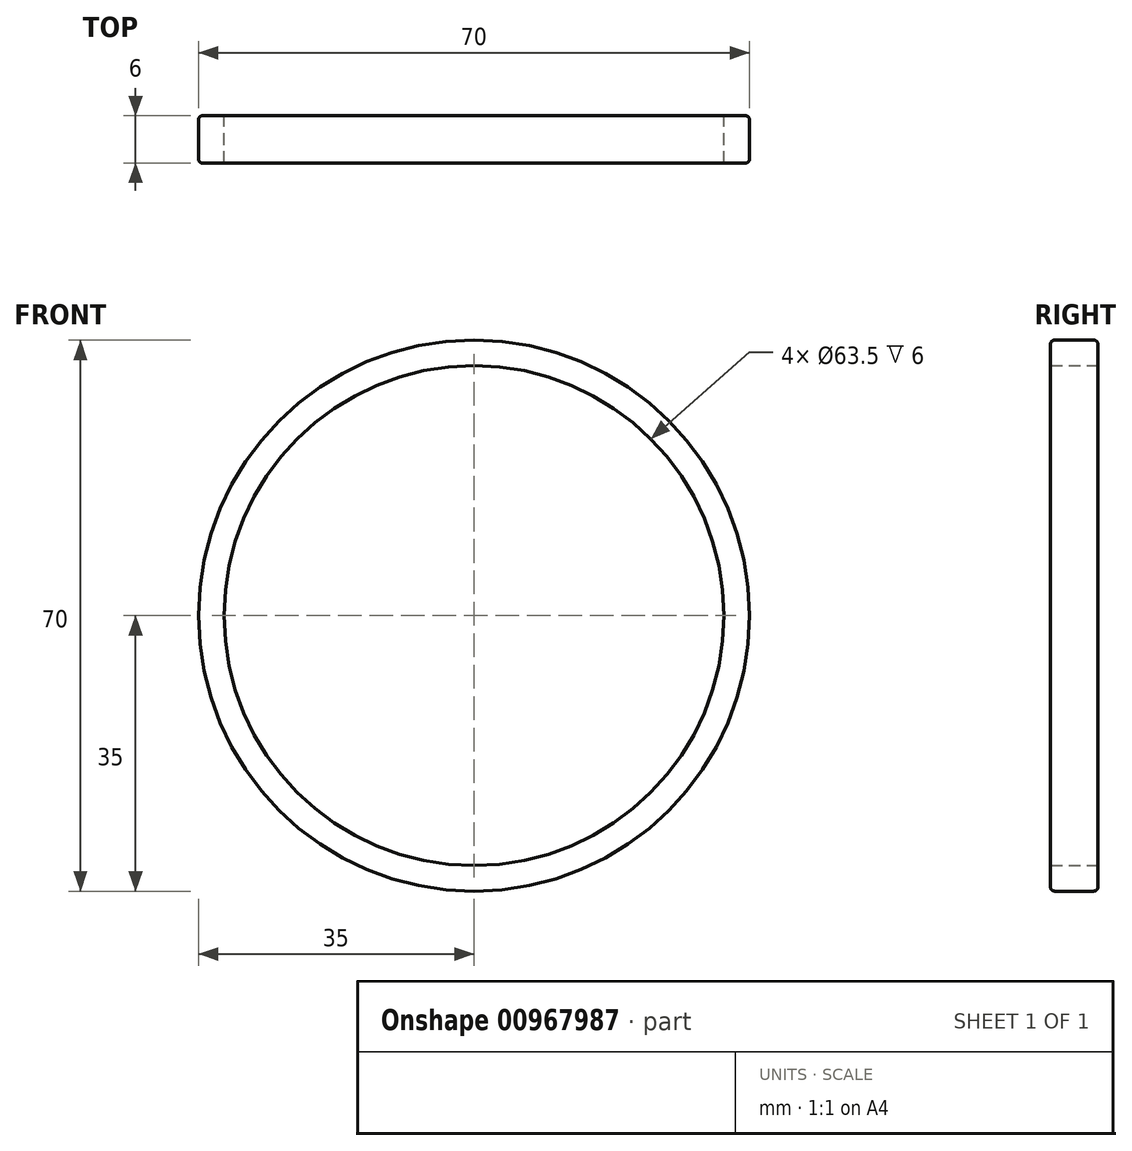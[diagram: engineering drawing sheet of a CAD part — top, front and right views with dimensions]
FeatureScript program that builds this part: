
annotation { "Feature Type Name" : "Feature", "Feature Type Description" : "" }
export const myFeature = defineFeature(function(context is Context, id is Id, definition is map)
    precondition{}
    {
        {
            var Q0;
            Q0=qCreatedBy(makeId("Front.planeOp"),FACE);
            var sketch = newSketch(context, id + "F0", { "sketchPlane" : qUnion([Q0])});
            skCircle(sketch, "E0", {"center": v(0, 0) * mm, "radius": 35 * mm});
            skCircle(sketch, "E1", {"center": v(0, 0) * mm, "radius": 31.75 * mm});
            skSolve(sketch);
        }
        {
            var Q0;
            Q0=makeQuery(id+"F0.imprint","IMPRINT",FACE,{"disambiguationData":[TD([[makeQuery(id+"F0.imprint","IMPRINT",EDGE,{"derivedFrom":sQuery(id+"F0.wireOp",EDGE,"E0")}),1.0]])]});
            extrude(context, id + "F1", {"entities" : qUnion([Q0]), "depth" : 6 * mm, "offsetDistance" : 25 * mm});
        }
        {
            var Q0;
            Q0=makeQuery(id+"F1.opExtrude","CAP_EDGE",EDGE,{"disambiguationData":[OSD([sQuery(id+"F0.wireOp",EDGE,"E0")])],"isStart":false});
            var Q1;
            Q1=makeQuery(id+"F1.opExtrude","CAP_EDGE",EDGE,{"disambiguationData":[OSD([sQuery(id+"F0.wireOp",EDGE,"E0")])],"isStart":true});
            fillet(context, id + "F2", {"entities" : qUnion([Q0, Q1]), "radius" : .5 * mm, "tangentPropagation" : true, "allowEdgeOverflow" : false});
        }
    });
